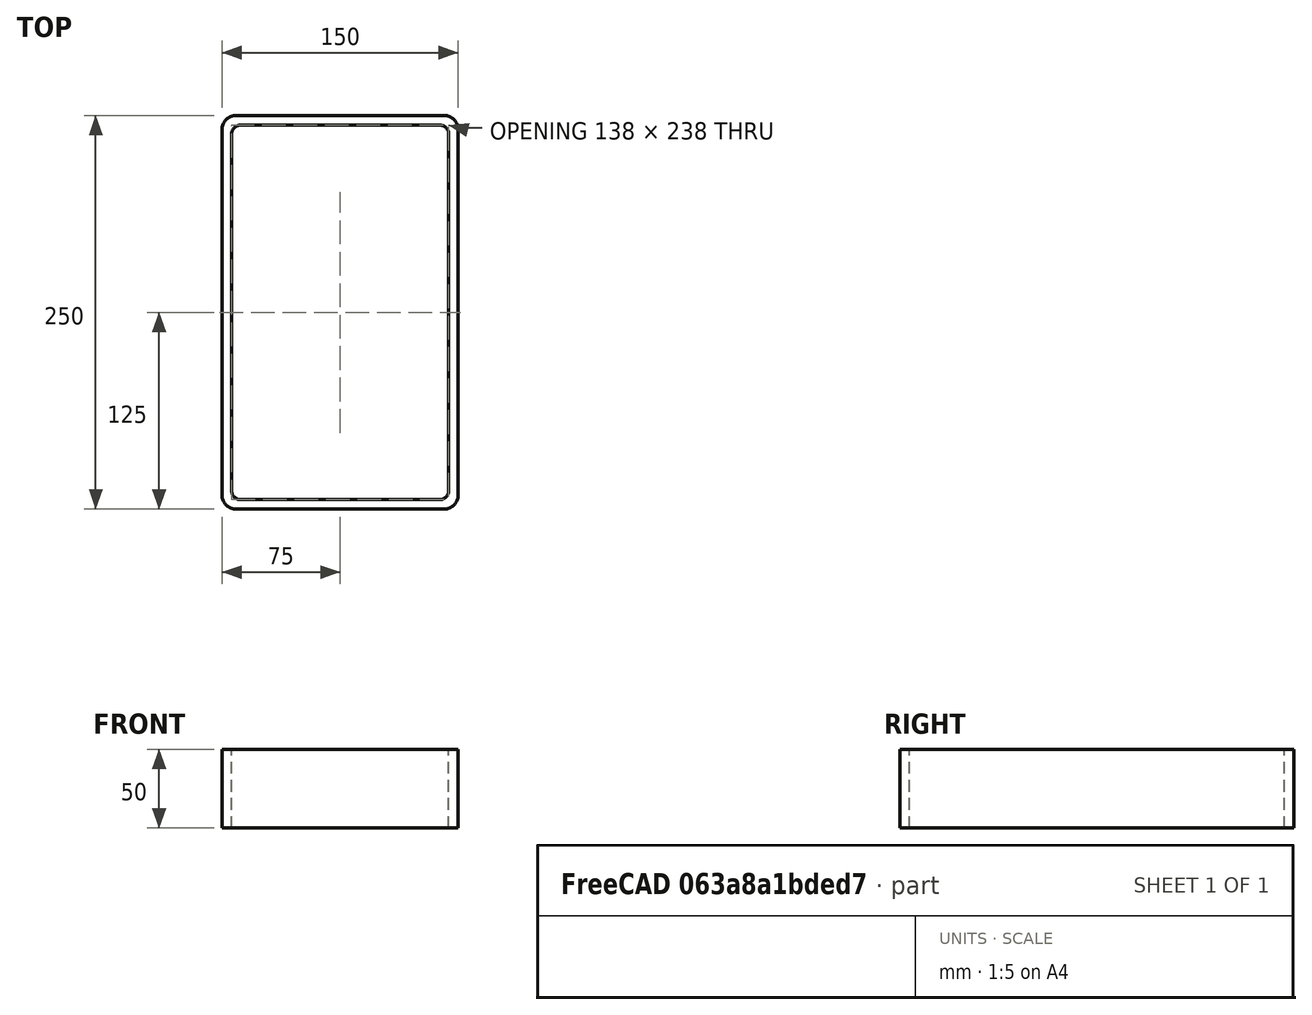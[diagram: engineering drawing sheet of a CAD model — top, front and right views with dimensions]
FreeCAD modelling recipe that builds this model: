
FCSTD DOCUMENT  (FreeCAD 0.15R4671 (Git))
Label: Rectangular hollow section 250x150x6 EN10219 S235JRH
License: All rights reserved
LicenseURL: http://en.wikipedia.org/wiki/All_rights_reserved
objects: Sketcher::SketchObject×1, Part::Extrusion×1
note: 2 computed .brp shape members not serialized (recipe doc carries the construction recipe); baked Part::Feature solids carry a one-line shape summary decoded from their .brp

FEATURE [Sketcher::SketchObject] Sketch
  sketch-geometry (16):
    g0: LineSegment StartX=-63 StartY=119 StartZ=0 EndX=63 EndY=119 EndZ=0
    g1: LineSegment StartX=69 StartY=113 StartZ=0 EndX=69 EndY=-113 EndZ=0
    g2: LineSegment StartX=63 StartY=-119 StartZ=0 EndX=-63 EndY=-119 EndZ=0
    g3: LineSegment StartX=-69 StartY=-113 StartZ=0 EndX=-69 EndY=113 EndZ=0
    g4: LineSegment StartX=-66 StartY=125 StartZ=0 EndX=66 EndY=125 EndZ=0
    g5: LineSegment StartX=75 StartY=116 StartZ=0 EndX=75 EndY=-116 EndZ=0
    g6: LineSegment StartX=66 StartY=-125 StartZ=0 EndX=-66 EndY=-125 EndZ=0
    g7: LineSegment StartX=-75 StartY=-116 StartZ=0 EndX=-75 EndY=116 EndZ=0
    g8: ArcOfCircle CenterX=-63 CenterY=113 CenterZ=0 NormalX=0 NormalY=0 NormalZ=1 Radius=6 StartAngle=1.5708 EndAngle=3.14159
    g9: ArcOfCircle CenterX=63 CenterY=113 CenterZ=0 NormalX=0 NormalY=0 NormalZ=1 Radius=6 StartAngle=0 EndAngle=1.5708
    g10: ArcOfCircle CenterX=63 CenterY=-113 CenterZ=0 NormalX=0 NormalY=0 NormalZ=1 Radius=6 StartAngle=4.71239 EndAngle=6.28319
    g11: ArcOfCircle CenterX=-63 CenterY=-113 CenterZ=0 NormalX=0 NormalY=0 NormalZ=1 Radius=6 StartAngle=3.14159 EndAngle=4.71239
    g12: ArcOfCircle CenterX=66 CenterY=116 CenterZ=0 NormalX=0 NormalY=0 NormalZ=1 Radius=9 StartAngle=0 EndAngle=1.5708
    g13: ArcOfCircle CenterX=66 CenterY=-116 CenterZ=0 NormalX=0 NormalY=0 NormalZ=1 Radius=9 StartAngle=4.71239 EndAngle=6.28319
    g14: ArcOfCircle CenterX=-66 CenterY=-116 CenterZ=0 NormalX=0 NormalY=0 NormalZ=1 Radius=9 StartAngle=3.14159 EndAngle=4.71239
    g15: ArcOfCircle CenterX=-66 CenterY=116 CenterZ=0 NormalX=0 NormalY=0 NormalZ=1 Radius=9 StartAngle=1.5708 EndAngle=3.14159
  constraints (36):
    c: Horizontal(g2)
    c: Vertical(g3)
    c: Horizontal(g6)
    c: Vertical(g7)
    c: Tangent(g3,g8) = 1.5708
    c: Tangent(g0,g8) = 1.5708
    c: Tangent(g0,g9) = 1.5708
    c: Tangent(g1,g9) = 1.5708
    c: Tangent(g1,g10) = 1.5708
    c: Tangent(g2,g10) = 1.5708
    c: Tangent(g2,g11) = 1.5708
    c: Tangent(g3,g11) = 1.5708
    c: Tangent(g4,g12) = 1.5708
    c: Tangent(g5,g12) = 1.5708
    c: Tangent(g5,g13) = 1.5708
    c: Tangent(g6,g13) = 1.5708
    c: Tangent(g6,g14) = 1.5708
    c: Tangent(g7,g14) = 1.5708
    c: Tangent(g7,g15) = 1.5708
    c: Tangent(g4,g15) = 1.5708
    c: Equal(g9,g8)
    c: Equal(g9,g11)
    c: Equal(g9,g10)
    c: Equal(g12,g15)
    c: Equal(g12,g14)
    c: Equal(g12,g13)
    c: Symmetric(g4,g6,g-1)
    c: Symmetric(g7,g5,g-2)
    c: DistanceY(g4,g6) = -250
    c: DistanceX(g7,g5) = 150
    c: Symmetric(g3,g1,g-2)
    c: Symmetric(g0,g2,g-1)
    c: DistanceY(g0,g4) = 6
    c: DistanceX(g5,g1) = -6
    c: Radius(g9) = 6
    c: Radius(g12) = 9
FEATURE [Part::Extrusion] Extrude  label="Rectangular hollow section 250x150x6 EN10219 S235JRH"
  Base = -> Sketch
  Dir = (0,0,50)
  Solid = true
